# Revit family: 400_ISR_TPN_multifunctioneel_opbouwarmatuur
name_source: partatom
category: Lighting Fixtures
revit_build: Autodesk Revit 2013 (Build: 20121003_2115(x64)
units: mm (PartAtom-declared; Revit-internal decimal feet)

## types (2) — shared parameters
Color Filter = 16777215
Dimming Lamp Color Temperature Shift = <None>
Emit from Line Length = 610 mm
Lamp = T5, TC-S, TC-L, LED
Lengte = 395 mm  [stored 1.29593 ft]
Manufacturer = Lightronics
Model = TPN
Photometric Web File = TPN-LLM4-1-7-D-F-531-230-X-X.ies
Tilt Angle = 90.00°
URL = http://www.lightronics.nl
Wattage Comments = 1 of 2 x 8 Watt, TC-S 1 of 2 x 9 Watt, TC-S 1 of 2 x 11 Watt, TC-L 1 of 2 x 18 Watt, LED 6,9 Watt, LED 12 Watt
nooduitgang = No
optioneel= vluchtwegaanduiding = No
vluchtweg_links = No
vluchtweg_onder = No
vluchtweg_rechts = No

## per-type parameters (varying)
| type | piramide_kap | standaard_kap |
| standaard kap | No | Yes |
| piramide kap | Yes | No |

note: [stored X ft] marks values corroborated as IEEE doubles in the binary element streams (Revit-internal decimal feet)

## geometry (parser evidence)
native form markers: Sweep x8
no freeform markers — native parametric forms only
